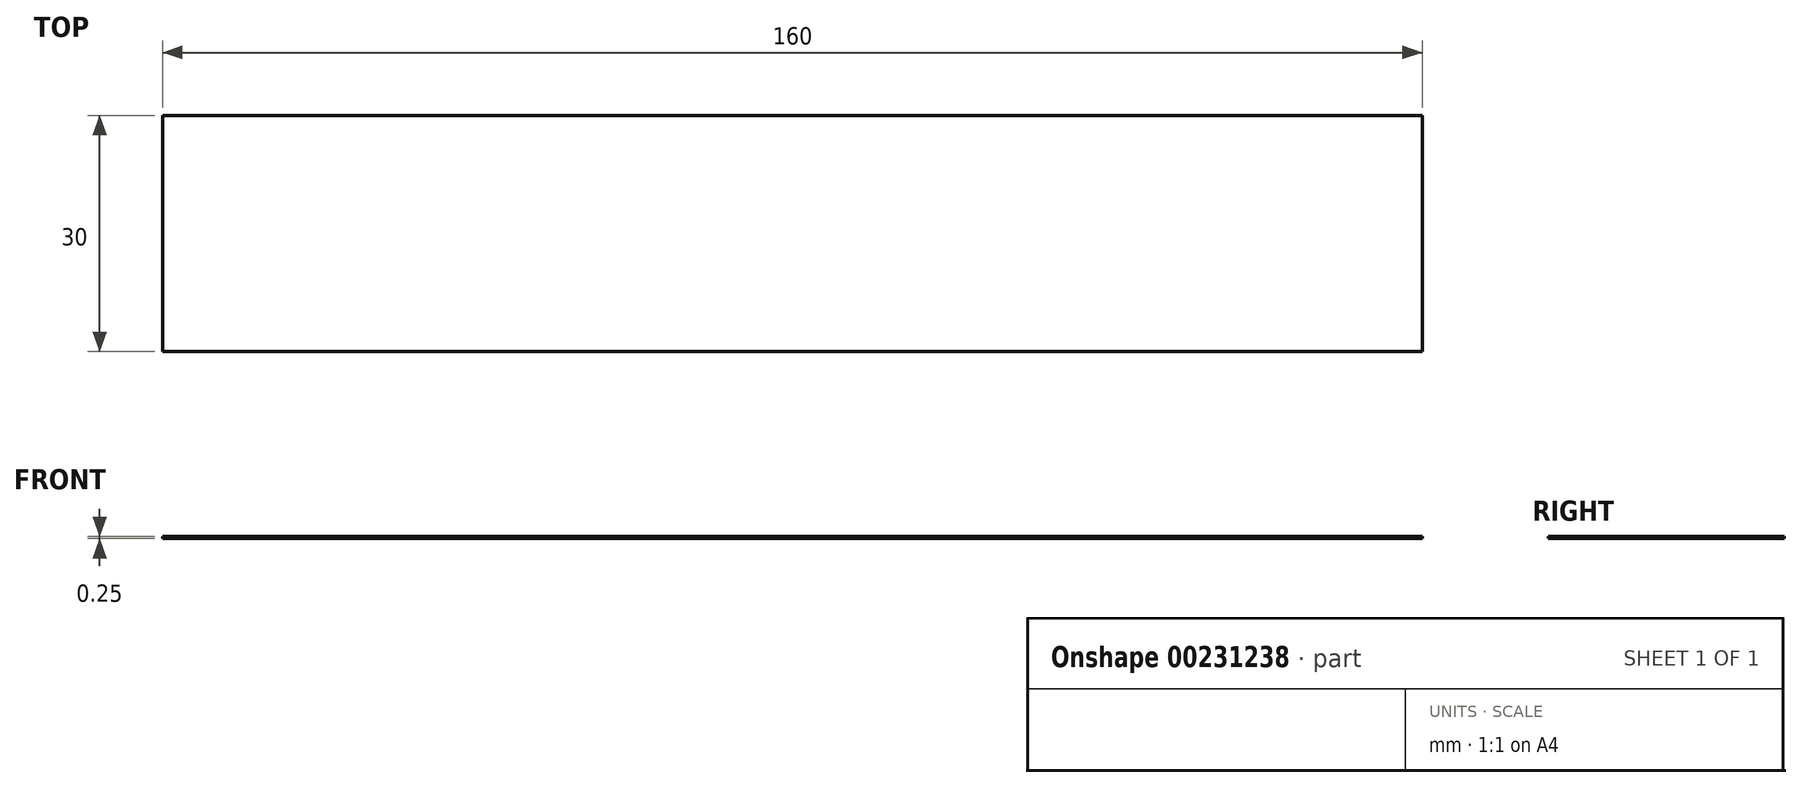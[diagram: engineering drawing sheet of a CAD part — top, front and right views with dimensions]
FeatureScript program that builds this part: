
annotation { "Feature Type Name" : "Feature", "Feature Type Description" : "" }
export const myFeature = defineFeature(function(context is Context, id is Id, definition is map)
    precondition{}
    {
        {
            var Q0;
            Q0=qCreatedBy(makeId("Top.planeOp"),FACE);
            var sketch = newSketch(context, id + "F0", { "sketchPlane" : qUnion([Q0])});
            skLineSegment(sketch, "E0.bottom", {"start": v(80, -15) * mm, "end": v(-80, -15) * mm});
            skLineSegment(sketch, "E0.top", {"start": v(80, 15) * mm, "end": v(-80, 15) * mm});
            skLineSegment(sketch, "E0.left", {"start": v(80, -15) * mm, "end": v(80, 15) * mm});
            skLineSegment(sketch, "E0.right", {"start": v(-80, -15) * mm, "end": v(-80, 15) * mm});
            skPoint(sketch, "E0.middle", {"position": v(0, 0) * mm});
            skLineSegment(sketch, "E1", {"start": v(-80, 0) * mm, "end": v(80, 0) * mm, "construction": true});
            skLineSegment(sketch, "E2", {"start": v(0, 15) * mm, "end": v(0, -15) * mm, "construction": true});
            skSolve(sketch);
        }
        {
            var Q0;
            Q0 = qSketchRegion(id + "F0", true);
            extrude(context, id + "F1", {"entities" : qUnion([Q0]), "depth" : 0.25 * mm});
        }
    });
